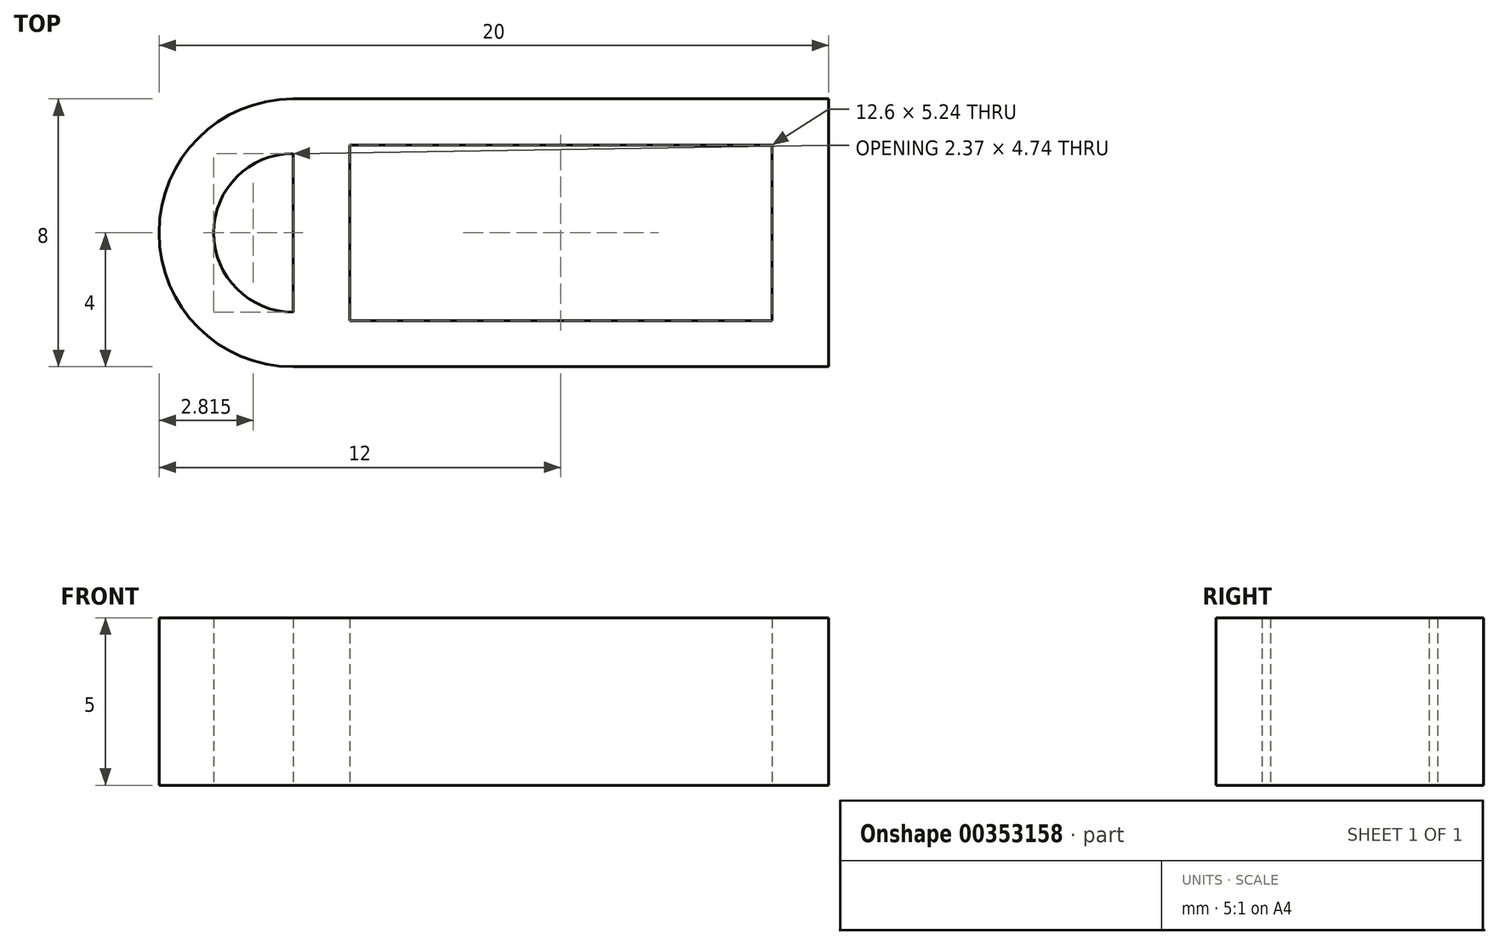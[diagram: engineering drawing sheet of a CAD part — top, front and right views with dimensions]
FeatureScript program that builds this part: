
annotation { "Feature Type Name" : "Feature", "Feature Type Description" : "" }
export const myFeature = defineFeature(function(context is Context, id is Id, definition is map)
    precondition{}
    {
        {
            var Q0;
            Q0=qCreatedBy(makeId("Top.planeOp"),FACE);
            var sketch = newSketch(context, id + "F0", { "sketchPlane" : qUnion([Q0])});
            skLineSegment(sketch, "E0.bottom", {"start": v(0, 4.74) * mm, "end": v(12.3, 4.74) * mm, "construction": true});
            skLineSegment(sketch, "E0.top", {"start": v(0, 0) * mm, "end": v(12.3, 0) * mm, "construction": true});
            skLineSegment(sketch, "E0.left", {"start": v(0, 4.74) * mm, "end": v(0, 0) * mm, "construction": true});
            skLineSegment(sketch, "E0.right", {"start": v(12.3, 4.74) * mm, "end": v(12.3, 0) * mm, "construction": true});
            skLineSegment(sketch, "E1.bottom", {"start": v(-0.15, 4.99) * mm, "end": v(12.45, 4.99) * mm});
            skLineSegment(sketch, "E1.top", {"start": v(-0.15, -0.25) * mm, "end": v(12.45, -0.25) * mm});
            skLineSegment(sketch, "E1.left", {"start": v(-0.15, 4.99) * mm, "end": v(-0.15, -0.25) * mm});
            skLineSegment(sketch, "E1.right", {"start": v(12.45, 4.99) * mm, "end": v(12.45, -0.25) * mm});
            skLineSegment(sketch, "E2.bottom", {"start": v(-1.85, -1.63) * mm, "end": v(14.15, -1.63) * mm});
            skLineSegment(sketch, "E2.top", {"start": v(-1.85, 6.37) * mm, "end": v(14.15, 6.37) * mm});
            skLineSegment(sketch, "E2.left", {"start": v(-1.85, 0) * mm, "end": v(-1.85, 4.74) * mm});
            skLineSegment(sketch, "E2.right", {"start": v(14.15, -1.63) * mm, "end": v(14.15, 6.37) * mm});
            skLineSegment(sketch, "E3", {"start": v(6.15, 4.74) * mm, "end": v(6.15, 6.37) * mm, "construction": true});
            skLineSegment(sketch, "E4", {"start": v(-1.85, 2.37) * mm, "end": v(0, 2.37) * mm, "construction": true});
            skArc(sketch, "E5", {"start": v(-1.85, 6.37) * mm, "mid": v(-5.85, 2.37) * mm, "end": v(-1.85, -1.63) * mm});
            skLineSegment(sketch, "E6", {"start": v(0, 0) * mm, "end": v(-1.85, 0) * mm, "construction": true});
            skLineSegment(sketch, "E7", {"start": v(0, 4.74) * mm, "end": v(-1.85, 4.74) * mm, "construction": true});
            skArc(sketch, "E8", {"start": v(-1.85, 4.74) * mm, "mid": v(-4.22, 2.37) * mm, "end": v(-1.85, 0) * mm});
            skSolve(sketch);
        }
        {
            var Q0;
            Q0=makeQuery(id+"F0.imprint","IMPRINT",FACE,{"disambiguationData":[TD([[makeQuery(id+"F0.imprint","IMPRINT",EDGE,{"derivedFrom":sQuery(id+"F0.wireOp",EDGE,"E0.bottom")}),1.0]])]});
            var Q1;
            Q1=makeQuery(id+"F0.imprint","IMPRINT",FACE,{"disambiguationData":[TD([[makeQuery(id+"F0.imprint","IMPRINT",EDGE,{"derivedFrom":sQuery(id+"F0.wireOp",EDGE,"E1.bottom")}),1.0]])]});
            extrude(context, id + "F1", {"entities" : qUnion([Q0, Q1]), "depth" : 5 * mm, "offsetDistance" : 25 * mm});
        }
    });
